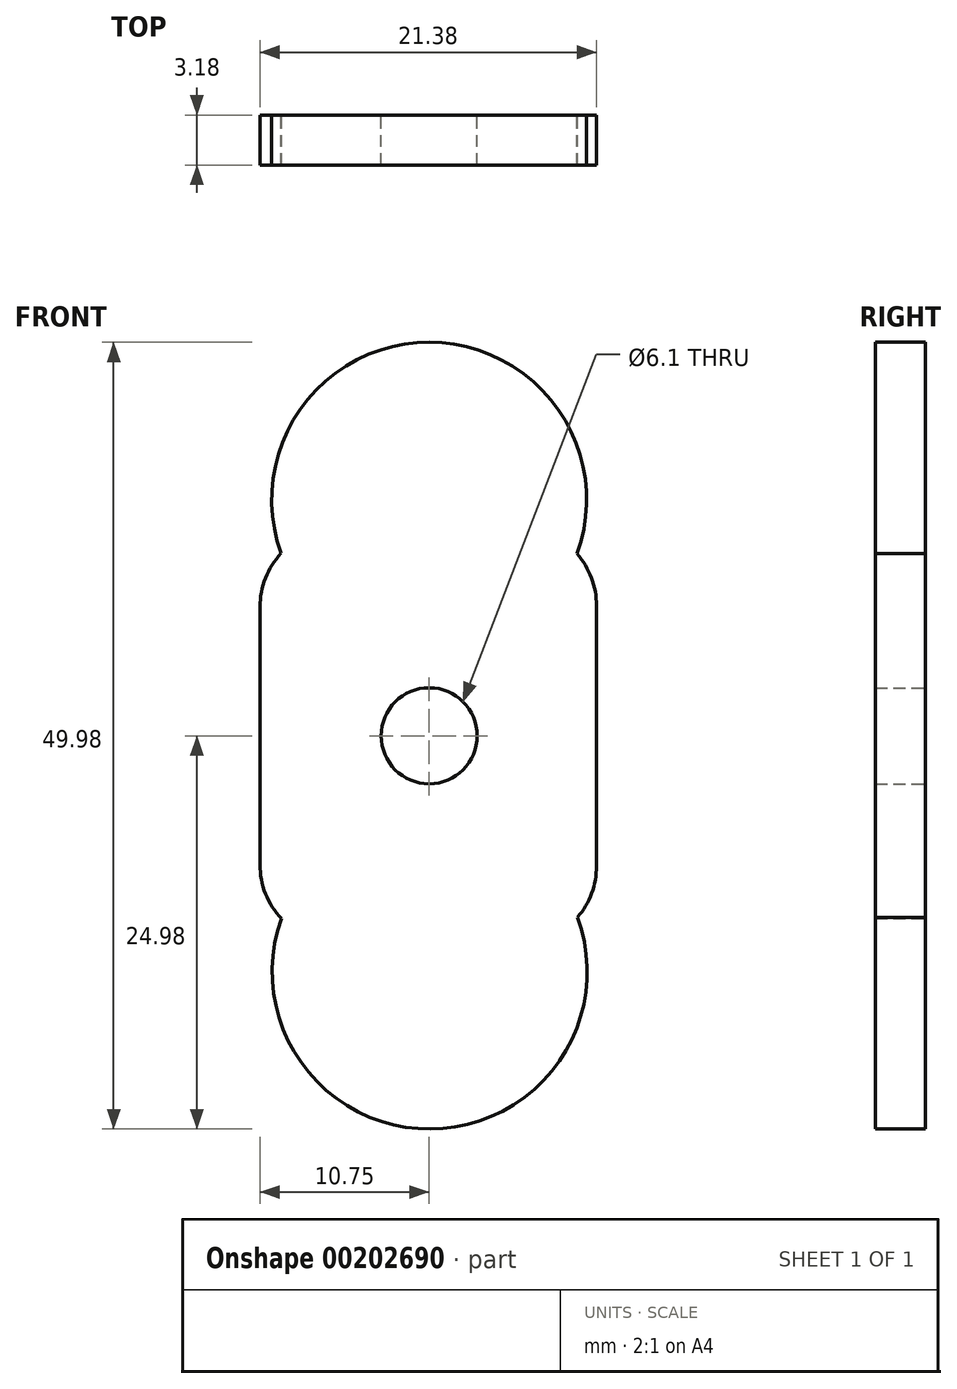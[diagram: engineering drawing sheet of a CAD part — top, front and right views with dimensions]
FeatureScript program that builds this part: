
annotation { "Feature Type Name" : "Feature", "Feature Type Description" : "" }
export const myFeature = defineFeature(function(context is Context, id is Id, definition is map)
    precondition{}
    {
        {
            var Q0;
            Q0=qCreatedBy(makeId("Front.planeOp"),FACE);
            var sketch = newSketch(context, id + "F0", { "sketchPlane" : qUnion([Q0])});
            skCircle(sketch, "E0", {"center": v(0, 0) * mm, "radius": 3.05 * mm});
            skArc(sketch, "E1", {"start": v(-8.62, -12.28) * mm, "mid": v(-0.1, -15) * mm, "end": v(8.45, -12.4) * mm});
            skLineSegment(sketch, "E2", {"start": v(0, 15) * mm, "end": v(0, -15) * mm});
            skCircle(sketch, "E3", {"center": v(0, 15) * mm, "radius": 10 * mm});
            skCircle(sketch, "E4", {"center": v(0.03, -14.98) * mm, "radius": 10 * mm});
            skLineSegment(sketch, "E5", {"start": v(-10.75, 8.18) * mm, "end": v(-10.75, -8.18) * mm});
            skLineSegment(sketch, "E6", {"start": v(10.63, 8.26) * mm, "end": v(10.63, -8.26) * mm});
            skArc(sketch, "E7.trimOffspring", {"start": v(8.45, 12.4) * mm, "mid": v(-0.1, 15) * mm, "end": v(-8.62, 12.28) * mm});
            skPoint(sketch, "E8.visualSharp", {"position": v(-10.75, 10.46) * mm});
            skArc(sketch, "E8.filletArc", {"start": v(-8.62, 12.28) * mm, "mid": v(-10.18, 10.49) * mm, "end": v(-10.75, 8.18) * mm});
            skPoint(sketch, "E9.visualSharp", {"position": v(-10.75, -10.46) * mm});
            skArc(sketch, "E9.filletArc", {"start": v(-10.75, -8.18) * mm, "mid": v(-10.18, -10.49) * mm, "end": v(-8.62, -12.28) * mm});
            skPoint(sketch, "E10.visualSharp", {"position": v(10.63, 10.58) * mm});
            skArc(sketch, "E10.filletArc", {"start": v(10.63, 8.26) * mm, "mid": v(10.05, 10.6) * mm, "end": v(8.45, 12.4) * mm});
            skPoint(sketch, "E11.visualSharp", {"position": v(10.63, -10.58) * mm});
            skArc(sketch, "E11.filletArc", {"start": v(8.45, -12.4) * mm, "mid": v(10.05, -10.6) * mm, "end": v(10.63, -8.26) * mm});
            skSolve(sketch);
        }
        {
            var Q0;
            Q0=makeQuery(id+"F0.imprint","IMPRINT",FACE,{"disambiguationData":[TD([[makeQuery(id+"F0.imprint","IMPRINT",EDGE,{"derivedFrom":sQuery(id+"F0.wireOp",EDGE,"E0")}),-1.0]])]});
            var Q1;
            {var subQ0=sQuery(id+"F0.wireOp",EDGE,"d85c369d-8d07-431c-96a2-927c0e74ee830.MirrorC");var subQ1=sQuery(id+"F0.wireOp",EDGE,"E1");var subQ2=makeQuery(id+"F0.imprint","INTERSECT",VERTEX,{"disambiguationData":[OD(0.0)],"derivedFrom":[subQ1,subQ0]});Q1=makeQuery(id+"F0.imprint","IMPRINT",FACE,{"disambiguationData":[TD([[makeQuery(id+"F0.imprint","IMPRINT",EDGE,{"disambiguationData":[TD([[subQ2,-1.0]])],"derivedFrom":subQ1}),-1.0]])]});}
            var Q2;
            {var subQ0=sQuery(id+"F0.wireOp",EDGE,"d85c369d-8d07-431c-96a2-927c0e74ee830.MirrorC");var subQ1=sQuery(id+"F0.wireOp",EDGE,"E1");var subQ2=makeQuery(id+"F0.imprint","INTERSECT",VERTEX,{"disambiguationData":[OD(0.0)],"derivedFrom":[subQ1,subQ0]});Q2=makeQuery(id+"F0.imprint","IMPRINT",FACE,{"disambiguationData":[TD([[makeQuery(id+"F0.imprint","IMPRINT",EDGE,{"disambiguationData":[TD([[subQ2,-1.0]])],"derivedFrom":subQ1}),1.0]])]});}
            var Q3;
            {var subQ0=sQuery(id+"F0.wireOp",EDGE,"FGQ64qtG-E2d3-lv1t-kFq6-JSFzmhOvakre");var subQ1=sQuery(id+"F0.wireOp",EDGE,"E1");var subQ2=makeQuery(id+"F0.imprint","INTERSECT",VERTEX,{"disambiguationData":[OD(0.0)],"derivedFrom":[subQ1,subQ0]});Q3=makeQuery(id+"F0.imprint","IMPRINT",FACE,{"disambiguationData":[TD([[makeQuery(id+"F0.imprint","IMPRINT",EDGE,{"disambiguationData":[TD([[subQ2,1.0]])],"derivedFrom":subQ1}),1.0]])]});}
            var Q4;
            {var subQ0=sQuery(id+"F0.wireOp",EDGE,"FGQ64qtG-E2d3-lv1t-kFq6-JSFzmhOvakre");var subQ1=sQuery(id+"F0.wireOp",EDGE,"E1");var subQ2=makeQuery(id+"F0.imprint","INTERSECT",VERTEX,{"disambiguationData":[OD(0.0)],"derivedFrom":[subQ1,subQ0]});Q4=makeQuery(id+"F0.imprint","IMPRINT",FACE,{"disambiguationData":[TD([[makeQuery(id+"F0.imprint","IMPRINT",EDGE,{"disambiguationData":[TD([[subQ2,1.0]])],"derivedFrom":subQ1}),-1.0]])]});}
            var Q5;
            {var subQ0=sQuery(id+"F0.wireOp",EDGE,"E7.trimOffspring");var subQ1=sQuery(id+"F0.wireOp",EDGE,"E2");var subQ2=makeQuery(id+"F0.imprint","INTERSECT",VERTEX,{"derivedFrom":[subQ1,subQ0]});Q5=makeQuery(id+"F0.imprint","IMPRINT",FACE,{"disambiguationData":[TD([[makeQuery(id+"F0.imprint","IMPRINT",EDGE,{"disambiguationData":[TD([[subQ2,-1.0]])],"derivedFrom":subQ1}),-1.0]])]});}
            var Q6;
            {var subQ0=sQuery(id+"F0.wireOp",EDGE,"E7.trimOffspring");var subQ1=sQuery(id+"F0.wireOp",EDGE,"E2");var subQ2=makeQuery(id+"F0.imprint","INTERSECT",VERTEX,{"derivedFrom":[subQ1,subQ0]});Q6=makeQuery(id+"F0.imprint","IMPRINT",FACE,{"disambiguationData":[TD([[makeQuery(id+"F0.imprint","IMPRINT",EDGE,{"disambiguationData":[TD([[subQ2,-1.0]])],"derivedFrom":subQ1}),1.0]])]});}
            var Q7;
            {var subQ0=sQuery(id+"F0.wireOp",EDGE,"E8.filletArc");var subQ3=sQuery(id+"F0.wireOp",EDGE,"E3");var subQ4=makeQuery(id+"F0.imprint","INTERSECT",VERTEX,{"derivedFrom":[subQ3,subQ0]});Q7=makeQuery(id+"F0.imprint","IMPRINT",FACE,{"disambiguationData":[TD([[makeQuery(id+"F0.imprint","IMPRINT",EDGE,{"disambiguationData":[TD([[subQ4,1.0]])],"derivedFrom":subQ3}),1.0]])]});}
            extrude(context, id + "F1", {"entities" : qUnion([Q0, Q1, Q2, Q3, Q4, Q5, Q6, Q7]), "depth" : 3.17 * mm});
        }
    });
